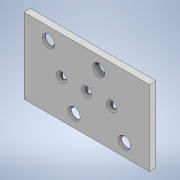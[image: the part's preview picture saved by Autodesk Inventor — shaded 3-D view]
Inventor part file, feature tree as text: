
AUTODESK INVENTOR PART (.ipt)
format: ipt  version: 2021 (Build 250183000, 183)  size: 299,008 bytes
history: native  units: in
note: dims shown in document units (in); Inventor stores cm internally (conversion verified against a paired STEP export)
features: projected_geometry x9, extrude x7, sketch x7, chamfer x2, pattern_linear x2
ambient origin geometry x8: Origin, YZ Plane, XZ Plane, XY Plane, X Axis, Y Axis, Z Axis, Center Point
bodies: Solid1 (feature_tree)
feature tree (27):
  extrude  "Extrusion1"  Depth=0.15in
  extrude  "Extrusion2"  Depth=0.239in
  extrude  "Extrusion3"  Depth=0.0071in TaperAngle=0.0deg
  chamfer  "Chamfer1"  Distance=0.0746in
  extrude  "Extrusion4"  Depth=0.05in
  extrude  "Extrusion5"  TaperAngle=0.0deg  [1 undecoded]
  pattern_linear  "Rectangular Pattern1"  Spacing1=0.004in  [1 undecoded]
  extrude  "Extrusion6"  Depth=0.3937in
  pattern_linear  "Rectangular Pattern2"  Spacing1=0.002in  [1 undecoded]
  chamfer  "Chamfer2"  Distance=0.0071in
  extrude  "Extrusion7"  Depth=0.3937in
  sketch  "Sketch1"  dims[d0=0.25in d1=0.15in]
  sketch  "Sketch2"  dims[d2=0.0059in d3=0.0in d4=0.239in]
  projected_geometry  "Projected Loop1"
  sketch  "Sketch3"  dims[d5=0.139in d6=0.0071in d7=0.0in]
  projected_geometry  "Projected Loop2"
  sketch  "Sketch4"  dims[d8=0.01in]
  sketch  "Sketch5"  dims[d9=0.0335in]
  projected_geometry  "Projected Loop3"
  sketch  "Sketch6"  dims[d10=0.7874in d12=0.0315in d13=0.3937in d15=1.0in]
  projected_geometry  "Projected Loop4"
  projected_geometry  "Projected Loop5"
  sketch  "Sketch7"  dims[d17=0.012in d18=0.0746in d19=1.1811in d21=0.05in d22=0.3937in d24=1.0in d26=0.0in d27=0.0in d28=0.004in d29=0.125in d30=45.0deg d31=0.002in d32=0.002in d33=0.0071in d34=0.0in d35=0.0236in d36=0.05in d37=0.05in d38=0.0in d39=0.0in d40=0.7874in d42=0.1in d43=0.7874in d45=0.076in d46=0.3937in d48=1.0in d52=0.01in d54=0.0565in d55=0.0071in d56=0.0in d57=1.1811in d59=0.05in d60=0.007in d61=0.125in d62=45.0deg d63=0.024in d64=0.7874in d66=0.1in d67=0.3937in d69=1.0in d71=0.0in d72=0.0in]
  projected_geometry  "Projected Loop6"
  projected_geometry  "Projected Loop7"
  projected_geometry  "Projected Loop8"
  projected_geometry  "Projected Loop9"
note: 3 required parameter values undecoded (feature->parameter linkage not recoverable at this tier; creation-order binding heuristic only, values carry confidence <= 0.55)
